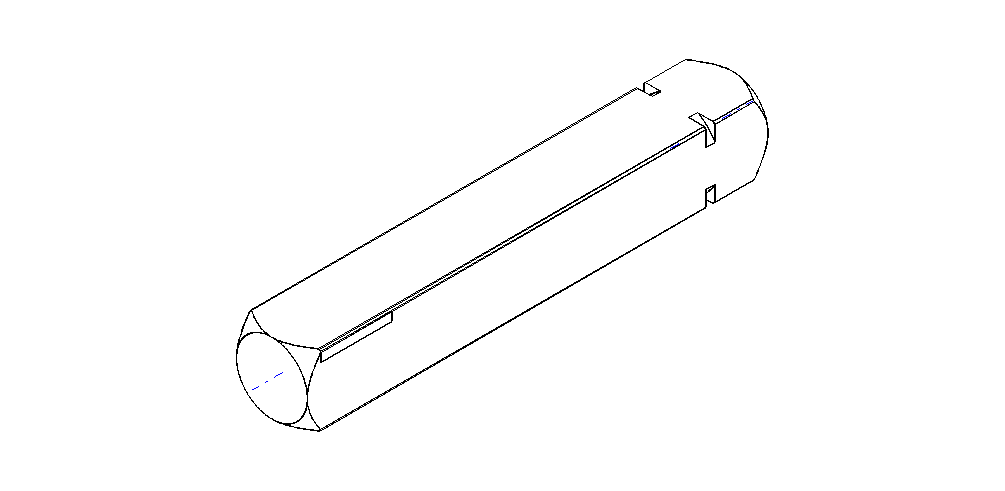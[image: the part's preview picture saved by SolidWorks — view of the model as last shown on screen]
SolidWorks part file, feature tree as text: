
SOLIDWORKS PART (.sldprt)
format: sldprt  version: not decoded by parser v0  size: 320,000 bytes
history: native  units: mm
features: sketch x8, plane x4, extrude x4, cut_extrude x3, chamfer x2, material x1 + 1 further entry (+10 scaffold rows collapsed)
feature tree (33):
  scaffold x10  (default folders/planes/origin — collapsed)
  material  "Matériau <non spécifié>"
  "Corps de surface"
  plane  "Face"
  plane  "Dessus"
  plane  "Droite"
  sketch  "Esquisse1"  dims[D1=8.0mm D2=8.0mm]
  extrude  "Base-Extrusion"  Depth=52mm
  sketch  "Esquisse2"
  cut_extrude  "Enlèv. mat.-Extru.1"  [1 undecoded]
  chamfer  "Chanfrein1"  Distance=0.2mm Angle=45deg
  sketch  "Esquisse3"  dims[D1=8.0mm]
  cut_extrude  "Enlèv. mat.-Extru.2"  [1 undecoded]
  plane  "Plan1"  Offset=6mm
  sketch  "Esquisse5"  dims[D1=9.0mm]
  cut_extrude  "Enlèv. mat.-Extru.4"  Depth=1mm
  sketch  "Esquisse6"  dims[D1=8.0mm D2=1.0mm]
  extrude  "Extrusion1"  Depth=0.01mm
  sketch  "Esquisse7"  dims[D1=1.0mm D2=8.0mm]
  chamfer  "Extrusion2"  Distance=0.01mm faceID=22
  extrude  "FaceIDTag-60"  Depth=60 faceID=60
  extrude  "FaceIDTag-65"  Depth=65 faceID=65
  sketch  "Esquisse8"  dims[D1=0.5mm D2=4.0mm]
  sketch  "Esquisse9"  dims[D1=4.0mm D2=0.5mm]
decode coverage: 14 of 17 modeling features carry decoded parameters; 1 rows unclassified (native names shown)
note: 2 parameter values undecoded
note: suppression state not decoded; provenance and decode notes live in map.json
